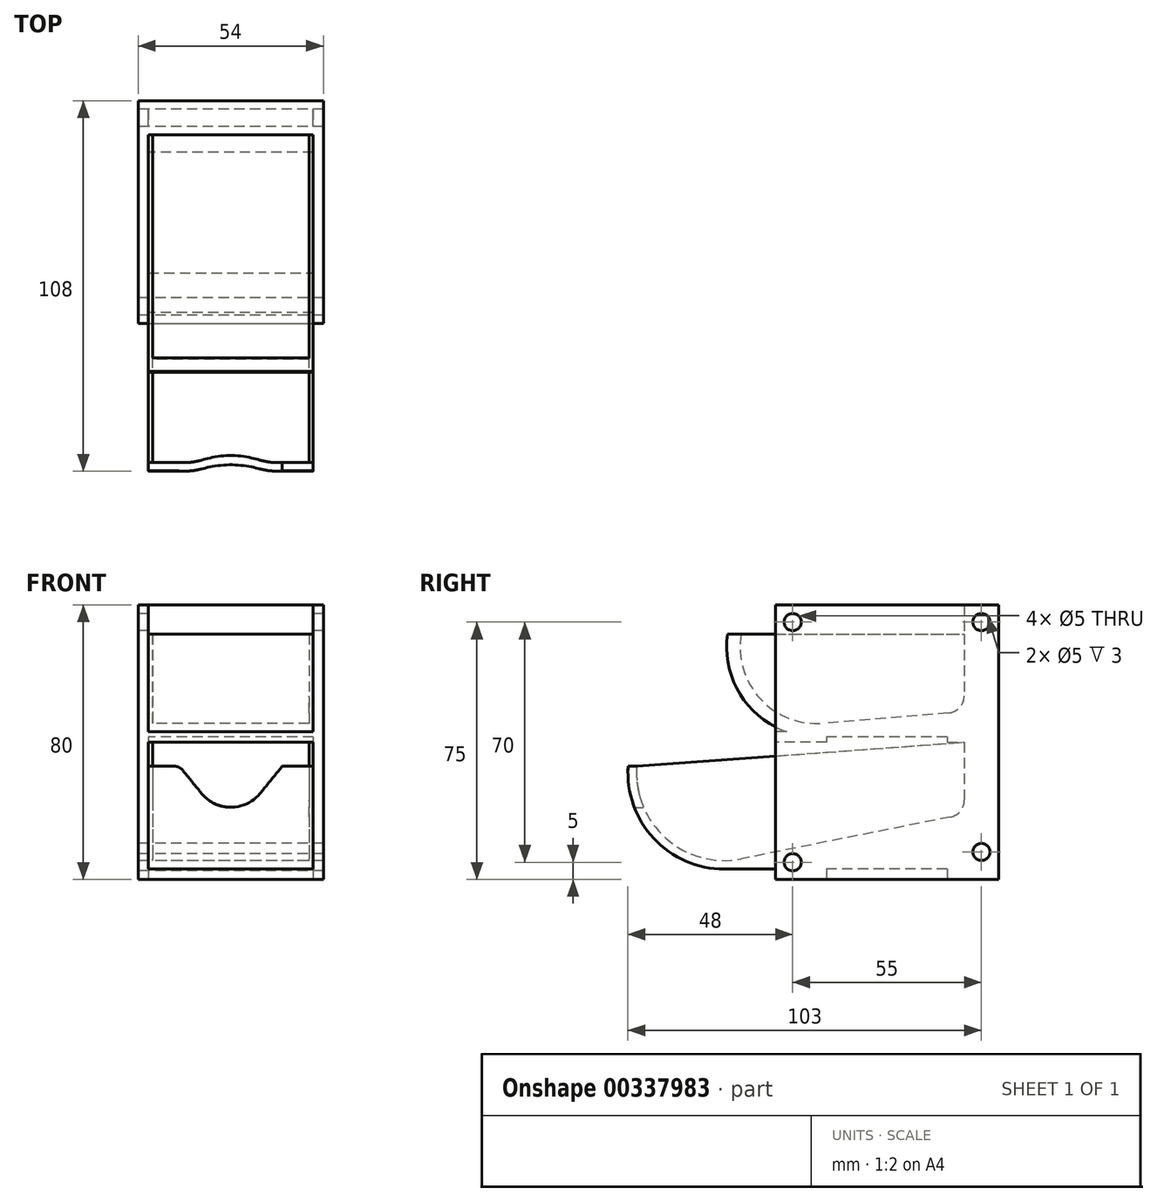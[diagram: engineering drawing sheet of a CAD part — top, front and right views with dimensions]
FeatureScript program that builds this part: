
annotation { "Feature Type Name" : "Feature", "Feature Type Description" : "" }
export const myFeature = defineFeature(function(context is Context, id is Id, definition is map)
    precondition{}
    {
        {
            var Q0;
            Q0=qCreatedBy(makeId("Top.planeOp"),FACE);
            var sketch = newSketch(context, id + "F0", { "sketchPlane" : qUnion([Q0])});
            skLineSegment(sketch, "E0", {"start": v(-27, 65) * mm, "end": v(-27, 0) * mm});
            skLineSegment(sketch, "E1", {"start": v(-27, 0) * mm, "end": v(27, 0) * mm});
            skLineSegment(sketch, "E2", {"start": v(27, 0) * mm, "end": v(27, 65) * mm});
            skLineSegment(sketch, "E3.0", {"start": v(-24, 65) * mm, "end": v(-24, 3) * mm});
            skLineSegment(sketch, "E4.0", {"start": v(-24, 3) * mm, "end": v(24, 3) * mm});
            skLineSegment(sketch, "E5.0", {"start": v(24, 3) * mm, "end": v(24, 65) * mm});
            skLineSegment(sketch, "E6", {"start": v(-27, 65) * mm, "end": v(-24, 65) * mm});
            skLineSegment(sketch, "E7", {"start": v(24, 65) * mm, "end": v(27, 65) * mm});
            skSolve(sketch);
        }
        {
            var Q0;
            Q0=qSketchRegion(id+"F0",true);
            extrude(context, id + "F1", {"entities" : qUnion([Q0]), "depth" : 80 * mm});
        }
        {
            var Q0;
            Q0=makeQuery(id+"F1.opExtrude","SWEPT_FACE",FACE,{"disambiguationData":[OSD([sQuery(id+"F0.wireOp",EDGE,"E1")])]});
            var sketch = newSketch(context, id + "F2", { "sketchPlane" : qUnion([Q0])});
            skLineSegment(sketch, "E8.bottom", {"start": v(-24, 3) * mm, "end": v(24, 3) * mm});
            skLineSegment(sketch, "E8.top", {"start": v(-24, 40) * mm, "end": v(24, 40) * mm});
            skLineSegment(sketch, "E8.left", {"start": v(-24, 3) * mm, "end": v(-24, 40) * mm});
            skLineSegment(sketch, "E8.right", {"start": v(24, 3) * mm, "end": v(24, 40) * mm});
            skLineSegment(sketch, "E9.bottom", {"start": v(-24, 80) * mm, "end": v(24, 80) * mm});
            skLineSegment(sketch, "E9.top", {"start": v(-24, 43) * mm, "end": v(24, 43) * mm});
            skLineSegment(sketch, "E9.left", {"start": v(-24, 80) * mm, "end": v(-24, 43) * mm});
            skLineSegment(sketch, "E9.right", {"start": v(24, 80) * mm, "end": v(24, 43) * mm});
            skSolve(sketch);
        }
        {
            var Q0;
            Q0=makeQuery(id+"F2.imprint","IMPRINT",FACE,{"disambiguationData":[TD([[makeQuery(id+"F2.imprint","IMPRINT",EDGE,{"derivedFrom":sQuery(id+"F2.wireOp",EDGE,"E8.bottom")}),1.0]])]});
            var Q1;
            Q1=makeQuery(id+"F2.imprint","IMPRINT",FACE,{"disambiguationData":[TD([[makeQuery(id+"F2.imprint","IMPRINT",EDGE,{"derivedFrom":sQuery(id+"F2.wireOp",EDGE,"E9.bottom")}),-1.0]])]});
            extrude(context, id + "F3", {"entities" : qUnion([Q0, Q1]), "operationType" : NewBodyOperationType.REMOVE, "endBound" : BoundingType.THROUGH_ALL, "oppositeDirection" : true, "depth" : 25 * mm});
        }
        {
            var Q0;
            {var subQ1=sQuery(id+"F0.wireOp",EDGE,"E4.0");Q0=makeQuery(id+"F3.boolean.opBoolean","SPLIT",FACE,{"disambiguationData":[TD([makeQuery(id+"F3.opExtrude","SWEPT_FACE",FACE,{"disambiguationData":[OSD([sQuery(id+"F2.wireOp",EDGE,"E8.bottom")])]})])],"derivedFrom":makeQuery(id+"F1.opExtrude","SWEPT_FACE",FACE,{"disambiguationData":[OSD([subQ1])]})});}
            extrude(context, id + "F4", {"entities" : qUnion([Q0]), "operationType" : NewBodyOperationType.ADD, "depth" : 11.8 * mm});
        }
        {
            var Q0;
            Q0=makeQuery(id+"F1.opExtrude","SWEPT_FACE",FACE,{"disambiguationData":[OSD([sQuery(id+"F0.wireOp",EDGE,"E7")])]});
            var sketch = newSketch(context, id + "F5", { "sketchPlane" : qUnion([Q0])});
            skLineSegment(sketch, "E10.bottom", {"start": v(-24, 3) * mm, "end": v(24, 3) * mm});
            skLineSegment(sketch, "E10.top", {"start": v(-24, 0) * mm, "end": v(24, 0) * mm});
            skLineSegment(sketch, "E11", {"start": v(-24, 3) * mm, "end": v(-24, 0) * mm});
            skLineSegment(sketch, "E12", {"start": v(24, 3) * mm, "end": v(24, 0) * mm});
            skSolve(sketch);
        }
        {
            var Q0;
            Q0=makeQuery(id+"F5.imprint","IMPRINT",FACE,{"disambiguationData":[TD([[makeQuery(id+"F5.imprint","IMPRINT",EDGE,{"derivedFrom":sQuery(id+"F5.wireOp",EDGE,"E10.bottom")}),-1.0]])]});
            extrude(context, id + "F6", {"entities" : qUnion([Q0]), "operationType" : NewBodyOperationType.ADD, "oppositeDirection" : true, "depth" : 15 * mm});
        }
        {
            var Q0;
            Q0=makeQuery(id+"F3.boolean.opBoolean","SPLIT",FACE,{"disambiguationData":[TD([makeQuery(id+"F3.opExtrude","SWEPT_FACE",FACE,{"disambiguationData":[OSD([sQuery(id+"F2.wireOp",EDGE,"E8.top")])]})])],"derivedFrom":makeQuery(id+"F1.opExtrude","SWEPT_FACE",FACE,{"disambiguationData":[OSD([sQuery(id+"F0.wireOp",EDGE,"E4.0")])]})});
            var Q1;
            Q1=makeQuery(id+"F4.opExtrude","CAP_FACE",FACE,{"disambiguationData":[OSD([sQuery(id+"F0.wireOp",EDGE,"E4.0")])],"isStart":false});
            extrude(context, id + "F7", {"entities" : qUnion([Q0]), "operationType" : NewBodyOperationType.ADD, "endBound" : BoundingType.UP_TO_SURFACE, "endBoundEntityFace" : qUnion([Q1]), "depth" : 25 * mm});
        }
        {
            var Q0;
            Q0=makeQuery(id+"F6.boolean.opBoolean","MERGE",FACE,{"derivedFrom":[makeQuery(id+"F1.opExtrude","SWEPT_FACE",FACE,{"disambiguationData":[OSD([sQuery(id+"F0.wireOp",EDGE,"E6")])]}),makeQuery(id+"F1.opExtrude","SWEPT_FACE",FACE,{"disambiguationData":[OSD([sQuery(id+"F0.wireOp",EDGE,"E7")])]}),makeQuery(id+"F6.opExtrude","CAP_FACE",FACE,{"disambiguationData":[OSD([sQuery(id+"F5.wireOp",EDGE,"E10.bottom"),sQuery(id+"F5.wireOp",EDGE,"E10.top"),sQuery(id+"F5.wireOp",EDGE,"E11"),sQuery(id+"F5.wireOp",EDGE,"E12")])],"isStart":true})]});
            var sketch = newSketch(context, id + "F8", { "sketchPlane" : qUnion([Q0])});
            skLineSegment(sketch, "E13.bottom", {"start": v(-24, 41.5) * mm, "end": v(24, 41.5) * mm});
            skLineSegment(sketch, "E13.top", {"start": v(-24, 40) * mm, "end": v(24, 40) * mm});
            skLineSegment(sketch, "E13.left", {"start": v(-24, 41.5) * mm, "end": v(-24, 40) * mm});
            skLineSegment(sketch, "E13.right", {"start": v(24, 41.5) * mm, "end": v(24, 40) * mm});
            skSolve(sketch);
        }
        {
            var Q0;
            Q0=makeQuery(id+"F8.imprint","IMPRINT",FACE,{"disambiguationData":[TD([[makeQuery(id+"F8.imprint","IMPRINT",EDGE,{"derivedFrom":sQuery(id+"F8.wireOp",EDGE,"E13.bottom")}),-1.0]])]});
            extrude(context, id + "F9", {"entities" : qUnion([Q0]), "operationType" : NewBodyOperationType.ADD, "oppositeDirection" : true, "depth" : 15 * mm});
        }
        {
            var Q0;
            Q0=qCreatedBy(makeId("Right.planeOp"),FACE);
            var sketch = newSketch(context, id + "F10", { "sketchPlane" : qUnion([Q0])});
            skLineSegment(sketch, "E14", {"start": v(65, 21) * mm, "end": v(65, 3) * mm});
            skLineSegment(sketch, "E15", {"start": v(65, 3) * mm, "end": v(-15, 3) * mm});
            skLineSegment(sketch, "E16", {"start": v(-42.93, 33) * mm, "end": v(-40.42, 33) * mm});
            skLineSegment(sketch, "E17", {"start": v(50.98, 18.2) * mm, "end": v(-10, 6) * mm});
            skArc(sketch, "E18", {"start": v(-10, 6) * mm, "mid": v(-31.93, 11.93) * mm, "end": v(-40.42, 33) * mm});
            skArc(sketch, "E19", {"start": v(-15, 3) * mm, "mid": v(-35.5, 11.92) * mm, "end": v(-42.93, 33) * mm});
            skPoint(sketch, "E20", {"position": v(0, 8) * mm});
            skLineSegment(sketch, "E21.bottom", {"start": v(55, 40) * mm, "end": v(65, 40) * mm});
            skLineSegment(sketch, "E21.top", {"start": v(55, 3) * mm, "end": v(65, 3) * mm});
            skLineSegment(sketch, "E21.left", {"start": v(55, 40) * mm, "end": v(55, 23.1) * mm});
            skLineSegment(sketch, "E21.right", {"start": v(65, 40) * mm, "end": v(65, 3) * mm});
            skPoint(sketch, "E22.visualSharp", {"position": v(55, 19) * mm});
            skArc(sketch, "E22.filletArc", {"start": v(50.98, 18.2) * mm, "mid": v(53.87, 19.93) * mm, "end": v(55, 23.1) * mm});
            skSolve(sketch);
        }
        {
            var Q0;
            Q0=makeQuery(id+"F10.imprint","IMPRINT",FACE,{"disambiguationData":[TD([[makeQuery(id+"F10.imprint","IMPRINT",EDGE,{"derivedFrom":sQuery(id+"F10.wireOp",EDGE,"E15")}),-1.0]])]});
            extrude(context, id + "F11", {"entities" : qUnion([Q0]), "endBound" : BoundingType.SYMMETRIC, "depth" : 48 * mm});
        }
        {
            var Q0;
            Q0=qCreatedBy(makeId("Right.planeOp"),FACE);
            var sketch = newSketch(context, id + "F12", { "sketchPlane" : qUnion([Q0])});
            skCircle(sketch, "E23", {"center": v(60, 75) * mm, "radius": 2.5 * mm});
            skCircle(sketch, "E24", {"center": v(60, 8) * mm, "radius": 2.5 * mm});
            skCircle(sketch, "E25", {"center": v(5, 75) * mm, "radius": 2.5 * mm});
            skCircle(sketch, "E26", {"center": v(5, 5) * mm, "radius": 2.5 * mm});
            skSolve(sketch);
        }
        {
            var Q0;
            Q0=qSketchRegion(id+"F12",true);
            extrude(context, id + "F13", {"entities" : qUnion([Q0]), "operationType" : NewBodyOperationType.REMOVE, "endBound" : BoundingType.SYMMETRIC, "depth" : 60 * mm});
        }
        {
            var Q0;
            Q0=qCreatedBy(makeId("Front.planeOp"),FACE);
            var sketch = newSketch(context, id + "F14", { "sketchPlane" : qUnion([Q0])});
            skArc(sketch, "E27", {"start": v(-8.53, 25.05) * mm, "mid": v(0, 21) * mm, "end": v(8.53, 25.05) * mm});
            skLineSegment(sketch, "E28", {"start": v(-15, 33) * mm, "end": v(-8.53, 25.05) * mm});
            skLineSegment(sketch, "E29", {"start": v(15, 33) * mm, "end": v(8.53, 25.05) * mm});
            skLineSegment(sketch, "E30", {"start": v(-15, 33) * mm, "end": v(15, 33) * mm});
            skSolve(sketch);
        }
        {
            var Q0;
            {var subQ3=sQuery(id+"F14.wireOp",EDGE,"E28");Q0=makeQuery(id+"F14.imprint","IMPRINT",FACE,{"disambiguationData":[TD([[makeQuery(id+"F14.imprint","IMPRINT",EDGE,{"derivedFrom":subQ3}),1.0]])]});}
            extrude(context, id + "F15", {"entities" : qUnion([Q0]), "operationType" : NewBodyOperationType.REMOVE, "endBound" : BoundingType.THROUGH_ALL, "depth" : 25 * mm});
        }
        {
            var Q0;
            {var subQ0=sQuery(id+"F14.wireOp",EDGE,"MtfT6Czh-sZGf-t5on-sXds-3ba3ZstzbUVo");var subQ1=sQuery(id+"F14.wireOp",EDGE,"E27");Q0=makeQuery(id+"F15.boolean.opBoolean","COPY",EDGE,{"derivedFrom":makeQuery(id+"F15.opExtrude","SWEPT_EDGE",EDGE,{"disambiguationData":[OSD([subQ1,subQ0]),TDD([makeQuery(id+"F14.imprint","INTERSECT",VERTEX,{"disambiguationData":[OD(1.0)],"derivedFrom":[subQ1,subQ0]})])]})});}
            var Q1;
            {var subQ0=sQuery(id+"F14.wireOp",EDGE,"MtfT6Czh-sZGf-t5on-sXds-3ba3ZstzbUVo");var subQ1=sQuery(id+"F14.wireOp",EDGE,"E27");Q1=makeQuery(id+"F15.boolean.opBoolean","COPY",EDGE,{"derivedFrom":makeQuery(id+"F15.opExtrude","SWEPT_EDGE",EDGE,{"disambiguationData":[OSD([subQ1,subQ0]),TDD([makeQuery(id+"F14.imprint","INTERSECT",VERTEX,{"disambiguationData":[OD(0.0)],"derivedFrom":[subQ1,subQ0]})])]})});}
            var Q2;
            Q2=makeQuery(id+"F15.boolean.opBoolean","COPY",EDGE,{"derivedFrom":makeQuery(id+"F15.opExtrude","SWEPT_EDGE",EDGE,{"disambiguationData":[OSD([sQuery(id+"F14.wireOp",EDGE,"E28"),sQuery(id+"F14.wireOp",EDGE,"E30")])]})});
            var Q3;
            Q3=makeQuery(id+"F15.boolean.opBoolean","COPY",EDGE,{"derivedFrom":makeQuery(id+"F15.opExtrude","SWEPT_EDGE",EDGE,{"disambiguationData":[OSD([sQuery(id+"F14.wireOp",EDGE,"E29"),sQuery(id+"F14.wireOp",EDGE,"E30")])]})});
            fillet(context, id + "F16", {"entities" : qUnion([Q0, Q1, Q2, Q3]), "radius" : 3.1 * mm, "tangentPropagation" : true, "allowEdgeOverflow" : false});
        }
        {
            var Q0;
            Q0=makeQuery(id+"F11.opExtrude","CAP_FACE",FACE,{"disambiguationData":[OSD([sQuery(id+"F10.wireOp",EDGE,"E15"),sQuery(id+"F10.wireOp",EDGE,"E16"),sQuery(id+"F10.wireOp",EDGE,"E17"),sQuery(id+"F10.wireOp",EDGE,"E18"),sQuery(id+"F10.wireOp",EDGE,"E19"),sQuery(id+"F10.wireOp",EDGE,"E21.bottom"),sQuery(id+"F10.wireOp",EDGE,"E21.top"),sQuery(id+"F10.wireOp",EDGE,"E21.left"),sQuery(id+"F10.wireOp",EDGE,"E21.right"),sQuery(id+"F10.wireOp",EDGE,"E22.filletArc")])],"isStart":false});
            var sketch = newSketch(context, id + "F17", { "sketchPlane" : qUnion([Q0])});
            skLineSegment(sketch, "E31", {"start": v(-10, 6) * mm, "end": v(50.98, 18.2) * mm});
            skArc(sketch, "E32", {"start": v(-10, 6) * mm, "mid": v(-31.93, 11.93) * mm, "end": v(-40.42, 33) * mm});
            skArc(sketch, "E33", {"start": v(50.98, 18.2) * mm, "mid": v(53.87, 19.93) * mm, "end": v(55, 23.1) * mm});
            skLineSegment(sketch, "E34", {"start": v(-40.42, 33) * mm, "end": v(55, 40) * mm});
            skLineSegment(sketch, "E35", {"start": v(55, 40) * mm, "end": v(55, 23.1) * mm});
            skSolve(sketch);
        }
        {
            var Q0;
            Q0=makeQuery(id+"F17.imprint","IMPRINT",FACE,{"disambiguationData":[TD([[makeQuery(id+"F17.imprint","IMPRINT",EDGE,{"derivedFrom":sQuery(id+"F17.wireOp",EDGE,"D6qSZE4Y-GkrM-nmcn-Q5eH-mDyn8alSTv53")}),-1.0]])]});
            var Q1;
            Q1=makeQuery(id+"F17.imprint","IMPRINT",FACE,{"disambiguationData":[TD([[makeQuery(id+"F17.imprint","IMPRINT",EDGE,{"derivedFrom":sQuery(id+"F17.wireOp",EDGE,"E31")}),-1.0]])]});
            extrude(context, id + "F18", {"entities" : qUnion([Q0, Q1]), "operationType" : NewBodyOperationType.ADD, "oppositeDirection" : true, "depth" : 1.2 * mm});
        }
        {
            var Q0;
            Q0=makeQuery(id+"F11.opExtrude","CAP_FACE",FACE,{"disambiguationData":[OSD([sQuery(id+"F10.wireOp",EDGE,"E15"),sQuery(id+"F10.wireOp",EDGE,"E16"),sQuery(id+"F10.wireOp",EDGE,"E17"),sQuery(id+"F10.wireOp",EDGE,"E18"),sQuery(id+"F10.wireOp",EDGE,"E19"),sQuery(id+"F10.wireOp",EDGE,"E21.bottom"),sQuery(id+"F10.wireOp",EDGE,"E21.top"),sQuery(id+"F10.wireOp",EDGE,"E21.left"),sQuery(id+"F10.wireOp",EDGE,"E21.right"),sQuery(id+"F10.wireOp",EDGE,"E22.filletArc")])],"isStart":true});
            var sketch = newSketch(context, id + "F19", { "sketchPlane" : qUnion([Q0])});
            skLineSegment(sketch, "E36", {"start": v(-50.98, 18.2) * mm, "end": v(10, 6) * mm});
            skArc(sketch, "E37", {"start": v(-50.98, 18.2) * mm, "mid": v(-53.87, 19.93) * mm, "end": v(-55, 23.1) * mm});
            skArc(sketch, "E38", {"start": v(10, 6) * mm, "mid": v(31.93, 11.93) * mm, "end": v(40.42, 33) * mm});
            skLineSegment(sketch, "E39", {"start": v(40.42, 33) * mm, "end": v(-55, 40) * mm});
            skLineSegment(sketch, "E40", {"start": v(-55, 40) * mm, "end": v(-55, 23.1) * mm});
            skSolve(sketch);
        }
        {
            var Q0;
            Q0=makeQuery(id+"F19.imprint","IMPRINT",FACE,{"disambiguationData":[TD([[makeQuery(id+"F19.imprint","IMPRINT",EDGE,{"derivedFrom":sQuery(id+"F19.wireOp",EDGE,"E36")}),1.0]])]});
            extrude(context, id + "F20", {"entities" : qUnion([Q0]), "operationType" : NewBodyOperationType.ADD, "oppositeDirection" : true, "depth" : 1.2 * mm});
        }
        {
            var Q0;
            Q0=qCreatedBy(makeId("Right.planeOp"),FACE);
            var sketch = newSketch(context, id + "F21", { "sketchPlane" : qUnion([Q0])});
            skLineSegment(sketch, "E41", {"start": v(55, 80) * mm, "end": v(55, 53.5) * mm});
            skLineSegment(sketch, "E42", {"start": v(55, 80) * mm, "end": v(65, 80) * mm});
            skLineSegment(sketch, "E43", {"start": v(65, 80) * mm, "end": v(65, 41.5) * mm});
            skLineSegment(sketch, "E44", {"start": v(65, 41.5) * mm, "end": v(12, 41.5) * mm});
            skPoint(sketch, "E45.visualSharp", {"position": v(55, 57.05) * mm});
            skArc(sketch, "E45.filletArc", {"start": v(50.41, 48.52) * mm, "mid": v(53.68, 50.11) * mm, "end": v(55, 53.5) * mm});
            skPoint(sketch, "E46", {"position": v(0, 46) * mm});
            skLineSegment(sketch, "E47", {"start": v(50.41, 48.52) * mm, "end": v(13.83, 45.5) * mm});
            skArc(sketch, "E48", {"start": v(13.83, 45.5) * mm, "mid": v(-4.45, 52.66) * mm, "end": v(-10, 71.5) * mm});
            skLineSegment(sketch, "E49", {"start": v(-10, 71.5) * mm, "end": v(-13.97, 71.5) * mm});
            skArc(sketch, "E50", {"start": v(12, 41.5) * mm, "mid": v(-7.84, 50.57) * mm, "end": v(-13.97, 71.5) * mm});
            skSolve(sketch);
        }
        {
            var Q0;
            Q0=makeQuery(id+"F21.imprint","IMPRINT",FACE,{"disambiguationData":[TD([[makeQuery(id+"F21.imprint","IMPRINT",EDGE,{"derivedFrom":sQuery(id+"F21.wireOp",EDGE,"E41")}),1.0]])]});
            extrude(context, id + "F22", {"entities" : qUnion([Q0]), "endBound" : BoundingType.SYMMETRIC, "depth" : 48 * mm});
        }
        {
            var Q0;
            Q0=makeQuery(id+"F22.opExtrude","CAP_FACE",FACE,{"disambiguationData":[OSD([sQuery(id+"F21.wireOp",EDGE,"E41"),sQuery(id+"F21.wireOp",EDGE,"E42"),sQuery(id+"F21.wireOp",EDGE,"E43"),sQuery(id+"F21.wireOp",EDGE,"E44"),sQuery(id+"F21.wireOp",EDGE,"E45.filletArc"),sQuery(id+"F21.wireOp",EDGE,"E47"),sQuery(id+"F21.wireOp",EDGE,"E48"),sQuery(id+"F21.wireOp",EDGE,"E49"),sQuery(id+"F21.wireOp",EDGE,"E50")])],"isStart":false});
            var sketch = newSketch(context, id + "F23", { "sketchPlane" : qUnion([Q0])});
            skLineSegment(sketch, "E51", {"start": v(-10, 71.5) * mm, "end": v(55, 71.5) * mm});
            skLineSegment(sketch, "E52", {"start": v(13.83, 45.5) * mm, "end": v(50.33, 48.51) * mm});
            skLineSegment(sketch, "E53", {"start": v(55, 71.5) * mm, "end": v(55, 53.5) * mm});
            skArc(sketch, "E54", {"start": v(-10, 71.5) * mm, "mid": v(-4.45, 52.66) * mm, "end": v(13.83, 45.5) * mm});
            skArc(sketch, "E55", {"start": v(50.41, 48.52) * mm, "mid": v(53.68, 50.11) * mm, "end": v(55, 53.5) * mm});
            skSolve(sketch);
        }
        {
            var Q0;
            Q0=makeQuery(id+"F23.imprint","IMPRINT",FACE,{"disambiguationData":[TD([[makeQuery(id+"F23.imprint","IMPRINT",EDGE,{"derivedFrom":sQuery(id+"F23.wireOp",EDGE,"E51")}),-1.0]])]});
            extrude(context, id + "F24", {"entities" : qUnion([Q0]), "operationType" : NewBodyOperationType.ADD, "oppositeDirection" : true, "depth" : 1.2 * mm});
        }
        {
            var Q0;
            Q0=makeQuery(id+"F22.opExtrude","CAP_FACE",FACE,{"disambiguationData":[OSD([sQuery(id+"F21.wireOp",EDGE,"E41"),sQuery(id+"F21.wireOp",EDGE,"E42"),sQuery(id+"F21.wireOp",EDGE,"E43"),sQuery(id+"F21.wireOp",EDGE,"E44"),sQuery(id+"F21.wireOp",EDGE,"E45.filletArc"),sQuery(id+"F21.wireOp",EDGE,"E47"),sQuery(id+"F21.wireOp",EDGE,"E48"),sQuery(id+"F21.wireOp",EDGE,"E49"),sQuery(id+"F21.wireOp",EDGE,"E50")])],"isStart":true});
            var sketch = newSketch(context, id + "F25", { "sketchPlane" : qUnion([Q0])});
            skLineSegment(sketch, "E56", {"start": v(10, 71.5) * mm, "end": v(-55, 71.5) * mm});
            skLineSegment(sketch, "E57", {"start": v(-55, 71.5) * mm, "end": v(-55, 53.5) * mm});
            skLineSegment(sketch, "E58", {"start": v(-50.41, 48.52) * mm, "end": v(-13.83, 45.5) * mm});
            skArc(sketch, "E59", {"start": v(-55, 53.5) * mm, "mid": v(-53.68, 50.11) * mm, "end": v(-50.41, 48.52) * mm});
            skArc(sketch, "E60", {"start": v(-13.83, 45.5) * mm, "mid": v(4.45, 52.66) * mm, "end": v(10, 71.5) * mm});
            skSolve(sketch);
        }
        {
            var Q0;
            Q0=makeQuery(id+"F25.imprint","IMPRINT",FACE,{"disambiguationData":[TD([[makeQuery(id+"F25.imprint","IMPRINT",EDGE,{"derivedFrom":sQuery(id+"F25.wireOp",EDGE,"E56")}),1.0]])]});
            extrude(context, id + "F26", {"entities" : qUnion([Q0]), "operationType" : NewBodyOperationType.ADD, "oppositeDirection" : true, "depth" : 1.2 * mm});
        }
    });
